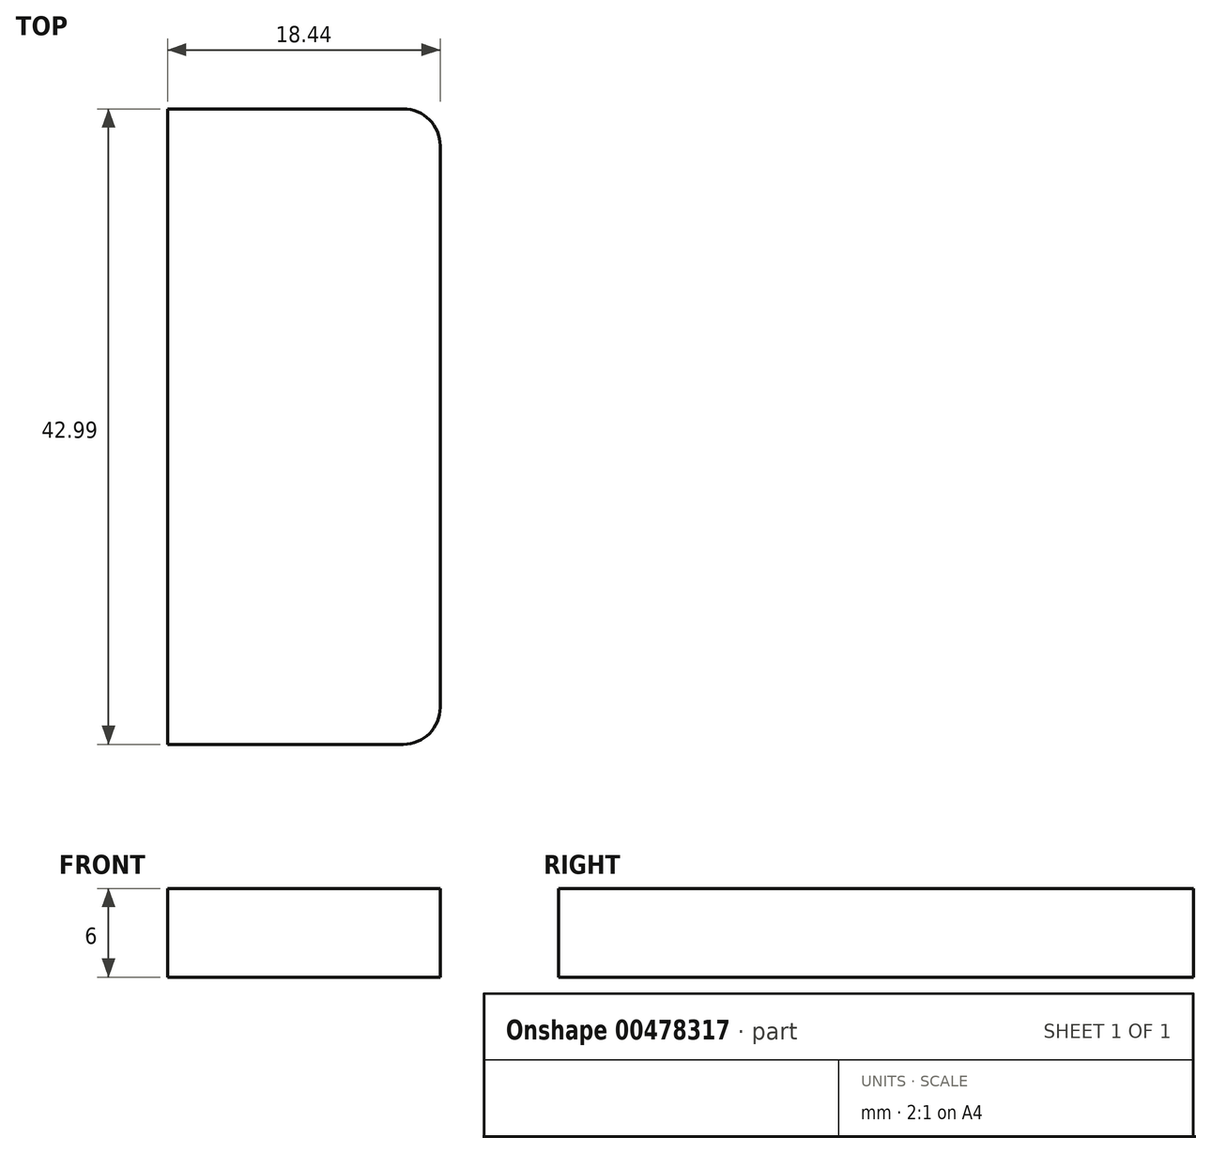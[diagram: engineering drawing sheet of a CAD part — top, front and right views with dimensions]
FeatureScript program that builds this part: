
annotation { "Feature Type Name" : "Feature", "Feature Type Description" : "" }
export const myFeature = defineFeature(function(context is Context, id is Id, definition is map)
    precondition{}
    {
        {
            var Q0;
            Q0=qCreatedBy(makeId("Top.planeOp"),FACE);
            var sketch = newSketch(context, id + "F0", { "sketchPlane" : qUnion([Q0])});
            skLineSegment(sketch, "E0.bottom", {"start": v(-22.81, 18.47) * mm, "end": v(-6.87, 18.47) * mm});
            skLineSegment(sketch, "E0.top", {"start": v(-22.81, -24.52) * mm, "end": v(-6.87, -24.52) * mm});
            skLineSegment(sketch, "E0.left", {"start": v(-22.81, 18.47) * mm, "end": v(-22.81, -24.52) * mm});
            skLineSegment(sketch, "E0.right", {"start": v(-4.37, 15.97) * mm, "end": v(-4.37, -22.02) * mm});
            skPoint(sketch, "E1.visualSharp", {"position": v(-22.81, 18.47) * mm});
            skLineSegment(sketch, "E1.filletArc", {"start": v(-22.81, 18.47) * mm, "end": v(-22.81, 18.47) * mm});
            skPoint(sketch, "E2.visualSharp", {"position": v(-4.37, 18.47) * mm});
            skArc(sketch, "E2.filletArc", {"start": v(-4.37, 15.97) * mm, "mid": v(-5.1, 17.73) * mm, "end": v(-6.87, 18.47) * mm});
            skPoint(sketch, "E3.visualSharp", {"position": v(-4.37, -24.52) * mm});
            skArc(sketch, "E3.filletArc", {"start": v(-6.87, -24.52) * mm, "mid": v(-5.1, -23.79) * mm, "end": v(-4.37, -22.02) * mm});
            skSolve(sketch);
        }
        {
            var Q0;
            Q0=makeQuery(id+"F0.imprint","IMPRINT",FACE,{"disambiguationData":[TD([[makeQuery(id+"F0.imprint","IMPRINT",EDGE,{"derivedFrom":sQuery(id+"F0.wireOp",EDGE,"E0.bottom")}),-1.0]])]});
            extrude(context, id + "F1", {"entities" : qUnion([Q0]), "depth" : 6 * mm});
        }
    });
